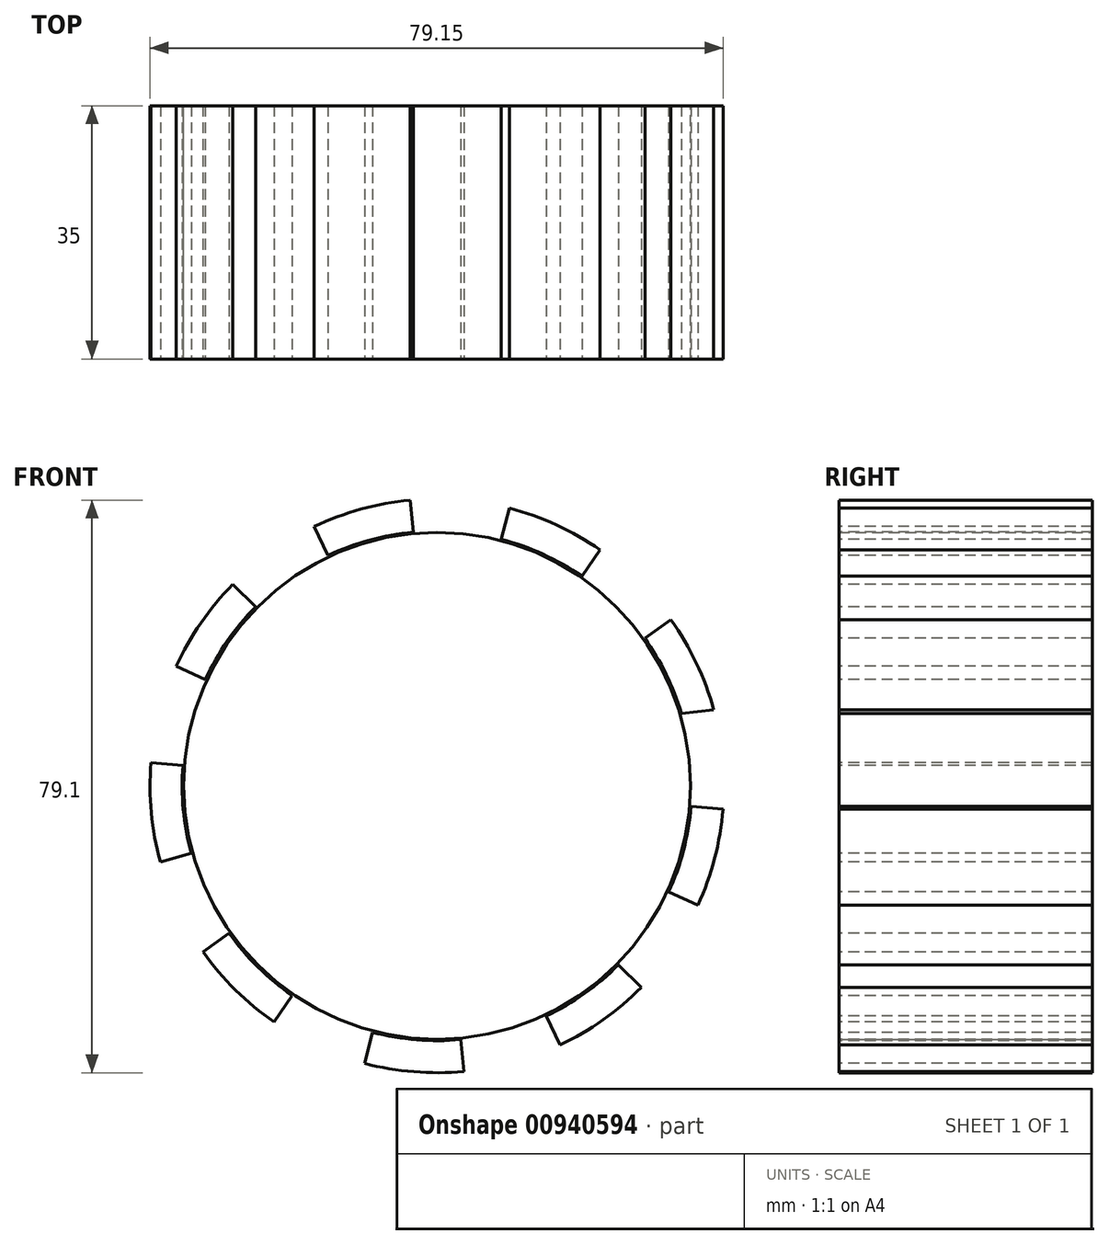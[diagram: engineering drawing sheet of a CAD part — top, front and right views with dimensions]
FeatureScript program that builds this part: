
annotation { "Feature Type Name" : "Feature", "Feature Type Description" : "" }
export const myFeature = defineFeature(function(context is Context, id is Id, definition is map)
    precondition{}
    {
        {
            var Q0;
            Q0=qCreatedBy(makeId("Front.planeOp"),FACE);
            var sketch = newSketch(context, id + "F0", { "sketchPlane" : qUnion([Q0])});
            skCircle(sketch, "E0", {"center": v(0, 0) * mm, "radius": 35 * mm});
            skSolve(sketch);
        }
        {
            var Q0;
            Q0=makeQuery(id+"F0.imprint","IMPRINT",FACE,{"disambiguationData":[TD([[makeQuery(id+"F0.imprint","IMPRINT",EDGE,{"derivedFrom":sQuery(id+"F0.wireOp",EDGE,"E0")}),1.0]])]});
            extrude(context, id + "F1", {"entities" : qUnion([Q0]), "depth" : 35 * mm, "offsetDistance" : 25.4 * mm});
        }
        {
            var Q0;
            Q0=makeQuery(id+"F1.opExtrude","CAP_FACE",FACE,{"disambiguationData":[OSD([sQuery(id+"F0.wireOp",EDGE,"E0")])],"isStart":false});
            var sketch = newSketch(context, id + "F2", { "sketchPlane" : qUnion([Q0])});
            skLineSegment(sketch, "E1.bottom", {"start": v(10, 10) * mm, "end": v(-10, 10) * mm});
            skLineSegment(sketch, "E1.top", {"start": v(10, -10) * mm, "end": v(-10, -10) * mm});
            skLineSegment(sketch, "E1.left", {"start": v(10, 10) * mm, "end": v(10, -10) * mm});
            skLineSegment(sketch, "E1.right", {"start": v(-10, 10) * mm, "end": v(-10, -10) * mm});
            skPoint(sketch, "E1.middle", {"position": v(0, 0) * mm});
            skSolve(sketch);
        }
        {
            var Q0;
            Q0=makeQuery(id+"F1.opExtrude","CAP_FACE",FACE,{"disambiguationData":[OSD([sQuery(id+"F0.wireOp",EDGE,"E0")])],"isStart":false});
            var sketch = newSketch(context, id + "F3", { "sketchPlane" : qUnion([Q0])});
            skCircle(sketch, "E2", {"center": v(0, 0) * mm, "radius": 35.2 * mm});
            skArc(sketch, "E3", {"start": v(22.52, 32.62) * mm, "mid": v(16.52, 36.03) * mm, "end": v(10, 38.35) * mm});
            skArc(sketch, "E4", {"start": v(-3.71, 39.46) * mm, "mid": v(-10.5, 38.22) * mm, "end": v(-16.98, 35.81) * mm});
            skArc(sketch, "E5", {"start": v(-28.2, 27.84) * mm, "mid": v(-32.62, 22.52) * mm, "end": v(-36.03, 16.52) * mm});
            skArc(sketch, "E6", {"start": v(-39.5, 3.2) * mm, "mid": v(-39.46, -3.71) * mm, "end": v(-38.22, -10.5) * mm});
            skArc(sketch, "E7", {"start": v(-32.32, -22.95) * mm, "mid": v(-27.84, -28.2) * mm, "end": v(-22.52, -32.62) * mm});
            skArc(sketch, "E8", {"start": v(-10, -38.35) * mm, "mid": v(-3.2, -39.5) * mm, "end": v(3.71, -39.46) * mm});
            skArc(sketch, "E9", {"start": v(16.98, -35.81) * mm, "mid": v(22.95, -32.32) * mm, "end": v(28.2, -27.84) * mm});
            skArc(sketch, "E10", {"start": v(36.03, -16.52) * mm, "mid": v(38.35, -10) * mm, "end": v(39.5, -3.2) * mm});
            skArc(sketch, "E11", {"start": v(38.22, 10.5) * mm, "mid": v(35.81, 16.98) * mm, "end": v(32.32, 22.95) * mm});
            skArc(sketch, "E12", {"start": v(19.89, 28.8) * mm, "mid": v(14.58, 31.82) * mm, "end": v(8.84, 33.87) * mm});
            skArc(sketch, "E13", {"start": v(-3.28, 34.85) * mm, "mid": v(-9.28, 33.75) * mm, "end": v(-15, 31.62) * mm});
            skArc(sketch, "E14", {"start": v(-24.9, 24.59) * mm, "mid": v(-28.8, 19.89) * mm, "end": v(-31.82, 14.58) * mm});
            skArc(sketch, "E15", {"start": v(-34.89, 2.82) * mm, "mid": v(-34.85, -3.28) * mm, "end": v(-33.75, -9.28) * mm});
            skArc(sketch, "E16", {"start": v(-28.7, -20.38) * mm, "mid": v(-24.73, -25.06) * mm, "end": v(-20, -28.97) * mm});
            skArc(sketch, "E17", {"start": v(-8.9, -34.07) * mm, "mid": v(-2.84, -35.1) * mm, "end": v(3.3, -35.05) * mm});
            skArc(sketch, "E18", {"start": v(15.09, -31.81) * mm, "mid": v(20.38, -28.7) * mm, "end": v(25.06, -24.73) * mm});
            skArc(sketch, "E19", {"start": v(31.82, -14.58) * mm, "mid": v(33.87, -8.84) * mm, "end": v(34.89, -2.82) * mm});
            skArc(sketch, "E20", {"start": v(33.54, 10) * mm, "mid": v(31.46, 15.34) * mm, "end": v(28.54, 20.26) * mm});
            skLineSegment(sketch, "E21", {"start": v(-28.2, 27.84) * mm, "end": v(-24.9, 24.59) * mm});
            skLineSegment(sketch, "E22", {"start": v(-16.98, 35.81) * mm, "end": v(-15, 31.62) * mm});
            skLineSegment(sketch, "E23", {"start": v(-3.71, 39.46) * mm, "end": v(-3.28, 34.85) * mm});
            skLineSegment(sketch, "E24", {"start": v(10, 38.35) * mm, "end": v(8.84, 33.87) * mm});
            skLineSegment(sketch, "E25", {"start": v(22.52, 32.62) * mm, "end": v(19.89, 28.8) * mm});
            skLineSegment(sketch, "E26", {"start": v(28.54, 20.26) * mm, "end": v(32.32, 22.95) * mm});
            skLineSegment(sketch, "E27", {"start": v(38.22, 10.5) * mm, "end": v(33.54, 10) * mm});
            skLineSegment(sketch, "E28", {"start": v(34.89, -2.82) * mm, "end": v(39.5, -3.2) * mm});
            skLineSegment(sketch, "E29", {"start": v(31.82, -14.58) * mm, "end": v(36.03, -16.52) * mm});
            skLineSegment(sketch, "E30", {"start": v(25.06, -24.73) * mm, "end": v(28.2, -27.84) * mm});
            skLineSegment(sketch, "E31", {"start": v(15.09, -31.81) * mm, "end": v(16.98, -35.81) * mm});
            skLineSegment(sketch, "E32", {"start": v(3.3, -35.05) * mm, "end": v(3.71, -39.46) * mm});
            skLineSegment(sketch, "E33", {"start": v(-8.9, -34.07) * mm, "end": v(-10, -38.35) * mm});
            skLineSegment(sketch, "E34", {"start": v(-20, -28.97) * mm, "end": v(-22.52, -32.62) * mm});
            skLineSegment(sketch, "E35", {"start": v(-32.32, -22.95) * mm, "end": v(-28.7, -20.38) * mm});
            skLineSegment(sketch, "E36", {"start": v(-33.75, -9.28) * mm, "end": v(-38.22, -10.5) * mm});
            skLineSegment(sketch, "E37", {"start": v(-39.5, 3.2) * mm, "end": v(-34.89, 2.82) * mm});
            skLineSegment(sketch, "E38", {"start": v(-36.03, 16.52) * mm, "end": v(-31.82, 14.58) * mm});
            skSolve(sketch);
        }
        {
            var Q0;
            {var subQ5=sQuery(id+"F3.wireOp",EDGE,"E7");Q0=makeQuery(id+"F3.imprint","IMPRINT",FACE,{"disambiguationData":[TD([[makeQuery(id+"F3.imprint","IMPRINT",EDGE,{"derivedFrom":subQ5}),1.0]])]});}
            var Q1;
            {var subQ5=sQuery(id+"F3.wireOp",EDGE,"E8");Q1=makeQuery(id+"F3.imprint","IMPRINT",FACE,{"disambiguationData":[TD([[makeQuery(id+"F3.imprint","IMPRINT",EDGE,{"derivedFrom":subQ5}),1.0]])]});}
            var Q2;
            {var subQ5=sQuery(id+"F3.wireOp",EDGE,"E9");Q2=makeQuery(id+"F3.imprint","IMPRINT",FACE,{"disambiguationData":[TD([[makeQuery(id+"F3.imprint","IMPRINT",EDGE,{"derivedFrom":subQ5}),1.0]])]});}
            var Q3;
            {var subQ5=sQuery(id+"F3.wireOp",EDGE,"E10");Q3=makeQuery(id+"F3.imprint","IMPRINT",FACE,{"disambiguationData":[TD([[makeQuery(id+"F3.imprint","IMPRINT",EDGE,{"derivedFrom":subQ5}),1.0]])]});}
            var Q4;
            {var subQ5=sQuery(id+"F3.wireOp",EDGE,"E11");Q4=makeQuery(id+"F3.imprint","IMPRINT",FACE,{"disambiguationData":[TD([[makeQuery(id+"F3.imprint","IMPRINT",EDGE,{"derivedFrom":subQ5}),1.0]])]});}
            var Q5;
            {var subQ5=sQuery(id+"F3.wireOp",EDGE,"E3");Q5=makeQuery(id+"F3.imprint","IMPRINT",FACE,{"disambiguationData":[TD([[makeQuery(id+"F3.imprint","IMPRINT",EDGE,{"derivedFrom":subQ5}),1.0]])]});}
            var Q6;
            {var subQ5=sQuery(id+"F3.wireOp",EDGE,"E4");Q6=makeQuery(id+"F3.imprint","IMPRINT",FACE,{"disambiguationData":[TD([[makeQuery(id+"F3.imprint","IMPRINT",EDGE,{"derivedFrom":subQ5}),1.0]])]});}
            var Q7;
            {var subQ5=sQuery(id+"F3.wireOp",EDGE,"E5");Q7=makeQuery(id+"F3.imprint","IMPRINT",FACE,{"disambiguationData":[TD([[makeQuery(id+"F3.imprint","IMPRINT",EDGE,{"derivedFrom":subQ5}),1.0]])]});}
            var Q8;
            {var subQ5=sQuery(id+"F3.wireOp",EDGE,"E6");Q8=makeQuery(id+"F3.imprint","IMPRINT",FACE,{"disambiguationData":[TD([[makeQuery(id+"F3.imprint","IMPRINT",EDGE,{"derivedFrom":subQ5}),1.0]])]});}
            extrude(context, id + "F4", {"entities" : qUnion([Q0, Q1, Q2, Q3, Q4, Q5, Q6, Q7, Q8]), "oppositeDirection" : true, "depth" : 35 * mm, "offsetDistance" : 25.4 * mm});
        }
    });
